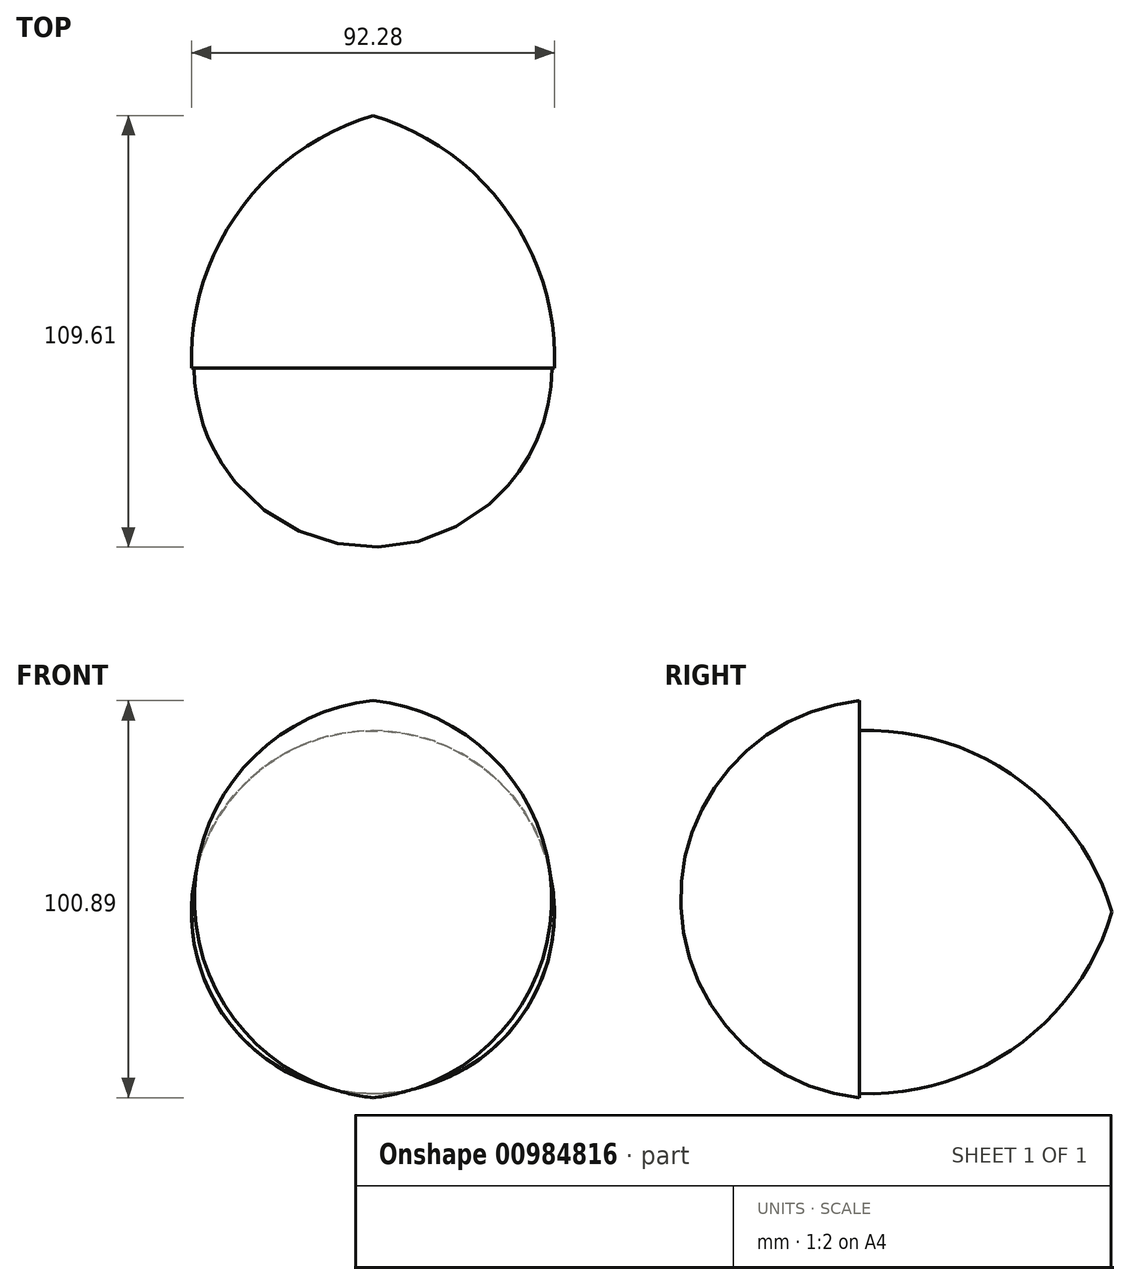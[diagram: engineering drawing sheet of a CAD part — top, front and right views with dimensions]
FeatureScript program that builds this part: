
annotation { "Feature Type Name" : "Feature", "Feature Type Description" : "" }
export const myFeature = defineFeature(function(context is Context, id is Id, definition is map)
    precondition{}
    {
        {
            var Q0;
            Q0=qCreatedBy(makeId("Front.planeOp"),FACE);
            var sketch = newSketch(context, id + "F0", { "sketchPlane" : qUnion([Q0])});
            skLineSegment(sketch, "E0", {"start": v(0, 53.75) * mm, "end": v(0, -47.14) * mm});
            skArc(sketch, "E1", {"start": v(0, -47.14) * mm, "mid": v(45.43, 3.3) * mm, "end": v(0, 53.75) * mm});
            skSolve(sketch);
        }
        {
            var Q0;
            Q0=makeQuery(id+"F0.imprint","IMPRINT",FACE,{"disambiguationData":[TD([[makeQuery(id+"F0.imprint","IMPRINT",EDGE,{"derivedFrom":sQuery(id+"F0.wireOp",EDGE,"E0")}),1.0]])]});
            var Q1;
            Q1=sQuery(id+"F0.wireOp",EDGE,"E0");
            revolve(context, id + "F1", {"surfaceOperationType" : NewSurfaceOperationType.NEW, "entities" : qUnion([Q0]), "axis" : qUnion([Q1]), "revolveType" : RevolveType.ONE_DIRECTION, "angle" : 180 * degree});
        }
        {
            var Q0;
            Q0=qCreatedBy(makeId("Top.planeOp"),FACE);
            var sketch = newSketch(context, id + "F2", { "sketchPlane" : qUnion([Q0])});
            skLineSegment(sketch, "E2", {"start": v(0, 0) * mm, "end": v(0, 64.18) * mm});
            skArc(sketch, "E3", {"start": v(46.1, 0) * mm, "mid": v(34.04, 39.98) * mm, "end": v(0, 64.18) * mm});
            skLineSegment(sketch, "E4", {"start": v(0, 64.18) * mm, "end": v(0, 0) * mm});
            skLineSegment(sketch, "E5", {"start": v(46.1, 0) * mm, "end": v(0, 0) * mm});
            skLineSegment(sketch, "E6.MirrorCS", {"start": v(-46.1, 0) * mm, "end": v(0, 0) * mm});
            skSolve(sketch);
        }
        {
            var Q0;
            Q0=makeQuery(id+"F2.imprint","IMPRINT",FACE,{"disambiguationData":[TD([[makeQuery(id+"F2.imprint","IMPRINT",EDGE,{"derivedFrom":sQuery(id+"F2.wireOp",EDGE,"E3")}),1.0]])]});
            var Q1;
            Q1=sQuery(id+"F2.wireOp",EDGE,"E4");
            revolve(context, id + "F3", {"operationType" : NewBodyOperationType.ADD, "surfaceOperationType" : NewSurfaceOperationType.NEW, "entities" : qUnion([Q0]), "axis" : qUnion([Q1]), "revolveType" : RevolveType.FULL});
        }
    });
